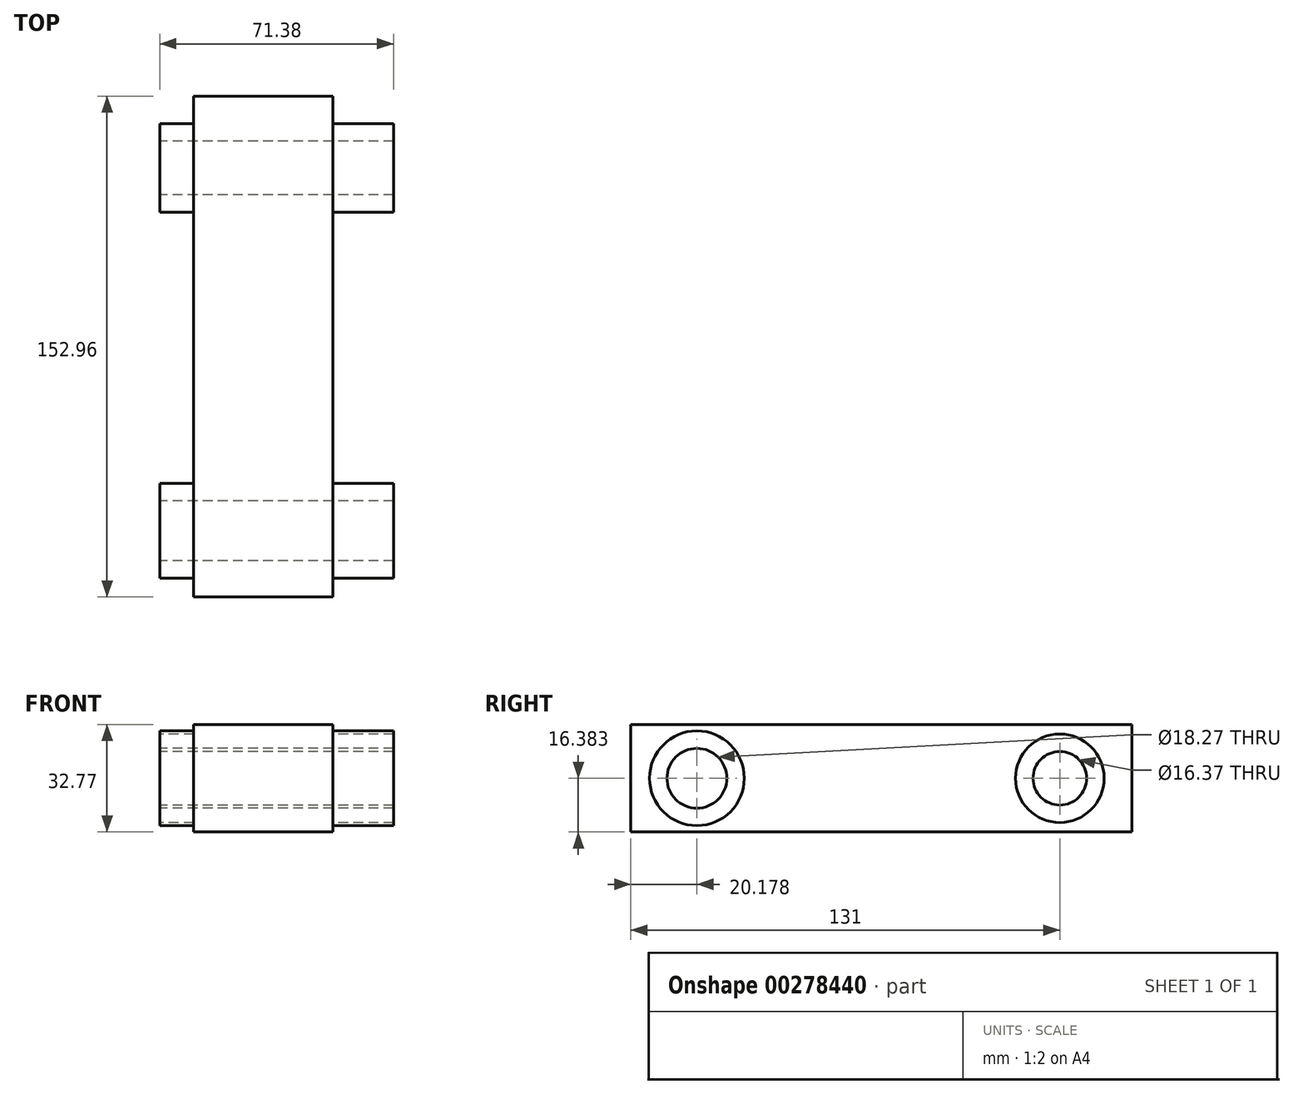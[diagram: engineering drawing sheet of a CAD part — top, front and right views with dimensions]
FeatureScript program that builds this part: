
annotation { "Feature Type Name" : "Feature", "Feature Type Description" : "" }
export const myFeature = defineFeature(function(context is Context, id is Id, definition is map)
    precondition{}
    {
        {
            var Q0;
            Q0=qCreatedBy(makeId("Top.planeOp"),FACE);
            var sketch = newSketch(context, id + "F0", { "sketchPlane" : qUnion([Q0])});
            skLineSegment(sketch, "E0.bottom", {"start": v(-21.22, -76.48) * mm, "end": v(21.22, -76.48) * mm});
            skLineSegment(sketch, "E0.top", {"start": v(-21.22, 76.48) * mm, "end": v(21.22, 76.48) * mm});
            skLineSegment(sketch, "E0.left", {"start": v(-21.22, -76.48) * mm, "end": v(-21.22, 76.48) * mm});
            skLineSegment(sketch, "E0.right", {"start": v(21.22, -76.48) * mm, "end": v(21.22, 76.48) * mm});
            skPoint(sketch, "E0.middle", {"position": v(0, 0) * mm});
            skSolve(sketch);
        }
        {
            var Q0;
            Q0=makeQuery(id+"F0.imprint","IMPRINT",FACE,{"disambiguationData":[TD([[makeQuery(id+"F0.imprint","IMPRINT",EDGE,{"derivedFrom":sQuery(id+"F0.wireOp",EDGE,"E0.bottom")}),1.0]])]});
            extrude(context, id + "F1", {"entities" : qUnion([Q0]), "depth" : 32.77 * mm});
        }
        {
            var Q0;
            Q0=makeQuery(id+"F1.opExtrude","SWEPT_FACE",FACE,{"disambiguationData":[OSD([sQuery(id+"F0.wireOp",EDGE,"E0.right")])]});
            var sketch = newSketch(context, id + "F2", { "sketchPlane" : qUnion([Q0])});
            skPoint(sketch, "E1", {"position": v(-76.48, 16.38) * mm});
            skPoint(sketch, "E2", {"position": v(76.48, 16.38) * mm});
            skLineSegment(sketch, "E3", {"start": v(-76.48, 16.38) * mm, "end": v(76.48, 16.38) * mm, "construction": true});
            skCircle(sketch, "E4", {"center": v(-56.3, 16.38) * mm, "radius": 14.47 * mm});
            skCircle(sketch, "E5", {"center": v(54.52, 16.38) * mm, "radius": 13.52 * mm});
            skCircle(sketch, "E6.0", {"center": v(-56.3, 16.38) * mm, "radius": 9.14 * mm});
            skCircle(sketch, "E7.0", {"center": v(54.52, 16.38) * mm, "radius": 8.19 * mm});
            skSolve(sketch);
        }
        {
            var Q0;
            Q0=makeQuery(id+"F2.imprint","IMPRINT",FACE,{"disambiguationData":[TD([[makeQuery(id+"F2.imprint","IMPRINT",EDGE,{"derivedFrom":sQuery(id+"F2.wireOp",EDGE,"E4")}),1.0]])]});
            var Q1;
            Q1=makeQuery(id+"F2.imprint","IMPRINT",FACE,{"disambiguationData":[TD([[makeQuery(id+"F2.imprint","IMPRINT",EDGE,{"derivedFrom":sQuery(id+"F2.wireOp",EDGE,"E5")}),1.0]])]});
            extrude(context, id + "F3", {"entities" : qUnion([Q0, Q1]), "operationType" : NewBodyOperationType.ADD, "depth" : 18.54 * mm, "hasSecondDirection" : true, "secondDirectionOppositeDirection" : true, "secondDirectionDepth" : 52.83 * mm});
        }
        {
            var Q0;
            Q0=makeQuery(id+"F3.boolean.opBoolean","SPLIT",FACE,{"disambiguationData":[TD([makeQuery(id+"F3.opExtrude","SWEPT_FACE",FACE,{"disambiguationData":[OSD([sQuery(id+"F2.wireOp",EDGE,"E7.0")])]})])],"derivedFrom":makeQuery(id+"F1.opExtrude","SWEPT_FACE",FACE,{"disambiguationData":[OSD([sQuery(id+"F0.wireOp",EDGE,"E0.right")])]})});
            var Q1;
            Q1=makeQuery(id+"F3.boolean.opBoolean","SPLIT",FACE,{"disambiguationData":[TD([makeQuery(id+"F3.opExtrude","SWEPT_FACE",FACE,{"disambiguationData":[OSD([sQuery(id+"F2.wireOp",EDGE,"E6.0")])]})])],"derivedFrom":makeQuery(id+"F1.opExtrude","SWEPT_FACE",FACE,{"disambiguationData":[OSD([sQuery(id+"F0.wireOp",EDGE,"E0.right")])]})});
            extrude(context, id + "F4", {"entities" : qUnion([Q0, Q1]), "operationType" : NewBodyOperationType.REMOVE, "endBound" : BoundingType.THROUGH_ALL, "oppositeDirection" : true, "depth" : 25.4 * mm});
        }
    });
